# Revit family: LAMP_B-SIDE 450
name_source: partatom
category: Luminarias
revit_build: Autodesk Revit LT 2015 (Build: 20140606_1530(x64)
units: mm (PartAtom-declared; Revit-internal decimal feet)

## types (4) — shared parameters
CRI = 80
Cambio de temperatura de color de luz atenuada = <Ninguno>
Diameter = 160 mm  [stored 0.524934 ft]
Elevación por defecto = 1219 mm
Fabricante = LAMP
Filtro de color = 16777215
Gear = Electronic
Height = 450 mm  [stored 1.47638 ft]
IEE = A++
Installation instructions = https://www.lamp.es
Insulation class = I
Last update = 21/12/2020
Luminaire type = Outdoor - Beacon
Lámpara = HIGH POWER LED
HIGH POWER LED
HIGH POWER LED
HIGH POWER LED
Manufacturer URL = http://www.lamp.es
Manufacturer country = Spain
Manufacturer name = LAMP
Power Supply = 110-240V 50-60Hz
Product URL = https://www.lamp.es
Product datasheet = http://www.lamp.es
Protection rating = IP65 / IK10
Type = HI POWER CREE
Ángulo de inclinación = 90.00°

## per-type parameters (varying)
| type | Archivo de red fotométrica | Descripción | Efficacy | Finish | LED Lifetime | MacAdam | Material | Modelo | Plum | Power | Product code | Weight |
| 93LM 4000 BLACK | 5841164.IES | B-SIDE LED 450 250 NW ANT. | 21 lm/W | Textured anthracite grey | 50.000 L70 B10 |  | LAMP_Aluminio B-Side antracita | BS1DB4503840NA | 5 W | 2 W | BS1DB4503840NA | 2.79 kg |
| 93LM 4000 GREY | 5841163.IES | B-SIDE LED 450 250 NW GR. | 21 lm/W | Texturised grey | 50.000 L70 B10 |  | LAMP_Aluminio B-Side gris | BS1DB4503840NG | 5 W | 2 W | BS1DB4503840NG | 2.79 kg |
| 130LM 4000 BLACK | 5841174_90.IES | B-SIDE LED 450 500 NW ANT. | 20 lm/W | Textured anthracite grey | 50.000 L90 | 4 | LAMP_Aluminio B-Side antracita | BS1DB4505840NA | 6 W | 5 W | BS1DB4505840NA | 2.45 kg |
| 130LM 4000 GREY | 5841173_90.IES | B-SIDE LED 450 500 NW GR. | 20 lm/W | Texturised grey | 50.000 L90 | 4 | LAMP_Aluminio B-Side gris | BS1DB4505840NG | 6 W | 5 W | BS1DB4505840NG | 2.45 kg |

note: [stored X ft] marks values corroborated as IEEE doubles in the binary element streams (Revit-internal decimal feet)
